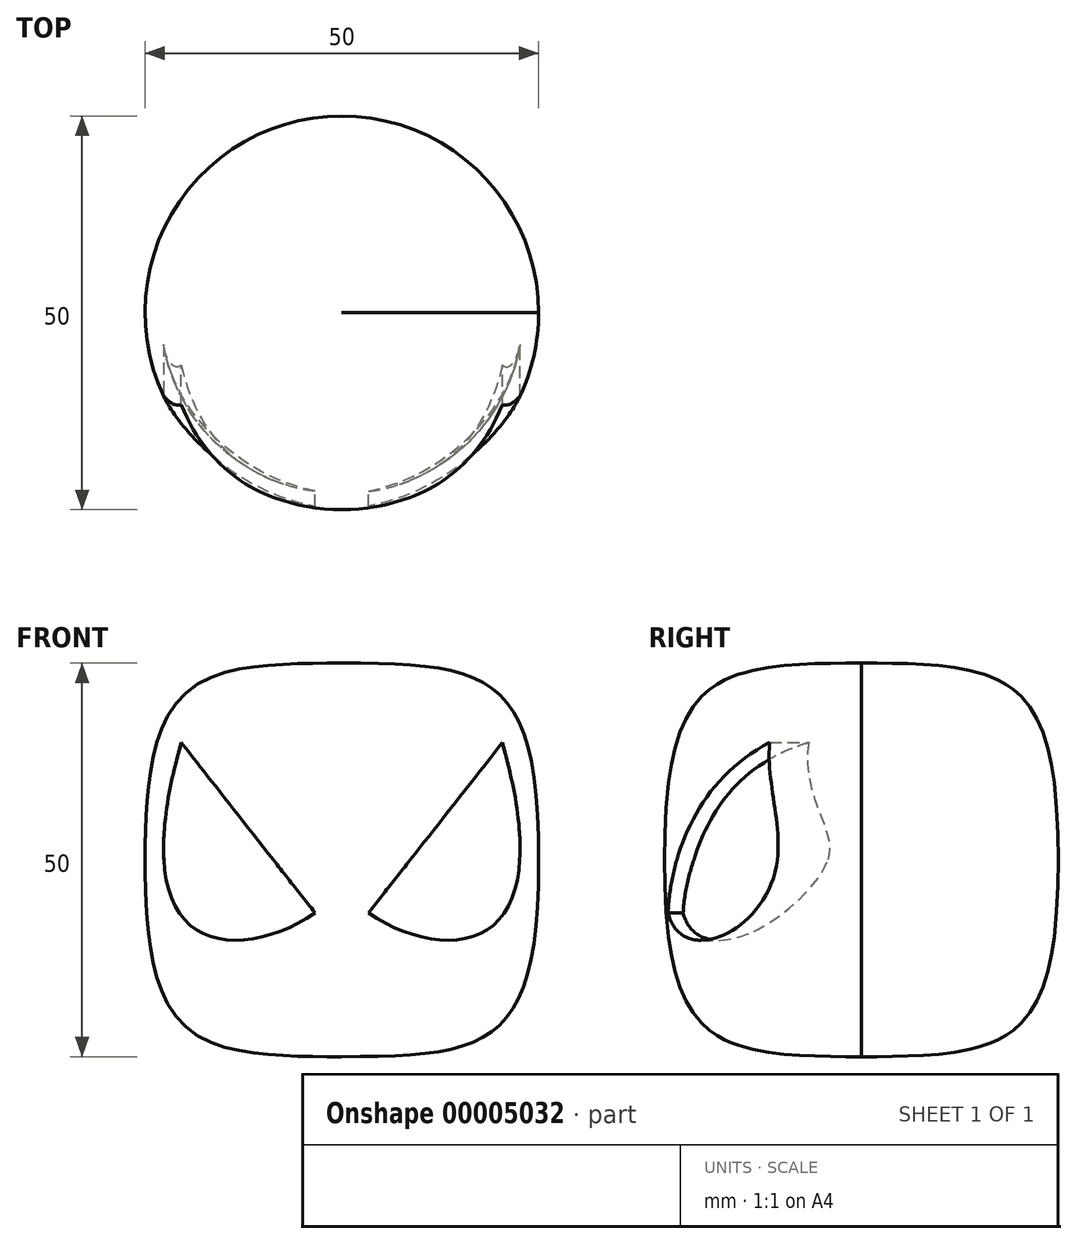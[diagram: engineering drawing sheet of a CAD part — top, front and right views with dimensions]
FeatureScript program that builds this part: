
annotation { "Feature Type Name" : "Feature", "Feature Type Description" : "" }
export const myFeature = defineFeature(function(context is Context, id is Id, definition is map)
    precondition{}
    {
        {
            var Q0;
            Q0=qCreatedBy(makeId("Front.planeOp"),FACE);
            var sketch = newSketch(context, id + "F0", { "sketchPlane" : qUnion([Q0])});
            skLineSegment(sketch, "E0", {"start": v(0, 0) * mm, "end": v(0, 25) * mm, "construction": true});
            skLineSegment(sketch, "E1", {"start": v(0, 0) * mm, "end": v(25, 0) * mm, "construction": true});
            skFitSpline(sketch, "E2", {"points": [v(0, 25) * mm, v(25, 0) * mm], "startDerivative": vector(56.82, 0) * mm, "endDerivative": vector(0, -71.1) * mm});
            skFitSpline(sketch, "E3.0.MirrorCS", {"points": [v(0, -25) * mm, v(25, 0) * mm], "startDerivative": vector(56.82, 0) * mm, "endDerivative": vector(0, 71.1) * mm});
            skLineSegment(sketch, "E4", {"start": v(0, 25) * mm, "end": v(0, -25) * mm});
            skFitSpline(sketch, "E5.0", {"points": [v(0, -23) * mm, v(2.36, -23) * mm, v(6.64, -22.96) * mm, v(10.94, -22.6) * mm, v(13.76, -22.06) * mm, v(15.56, -21.5) * mm, v(17.08, -20.78) * mm, v(18.34, -19.9) * mm, v(19.42, -18.8) * mm, v(20.36, -17.41) * mm, v(21.17, -15.66) * mm, v(22.07, -12.77) * mm, v(22.81, -8.04) * mm, v(23, -2.92) * mm, v(23, 0) * mm]});
            skFitSpline(sketch, "E5.1", {"points": [v(0, 23) * mm, v(2.36, 23) * mm, v(6.64, 22.96) * mm, v(10.94, 22.6) * mm, v(13.76, 22.06) * mm, v(15.56, 21.5) * mm, v(17.08, 20.78) * mm, v(18.34, 19.9) * mm, v(19.42, 18.8) * mm, v(20.36, 17.41) * mm, v(21.17, 15.66) * mm, v(22.07, 12.77) * mm, v(22.81, 8.04) * mm, v(23, 2.92) * mm, v(23, 0) * mm]});
            skSolve(sketch);
        }
        {
            var Q0;
            {var subQ1=sQuery(id+"F0.wireOp",EDGE,"E5.0");Q0=makeQuery(id+"F0.imprint","IMPRINT",FACE,{"disambiguationData":[TD([[makeQuery(id+"F0.imprint","IMPRINT",EDGE,{"derivedFrom":subQ1}),1.0]])]});}
            var Q1;
            {var subQ4=sQuery(id+"F0.wireOp",EDGE,"E2");Q1=makeQuery(id+"F0.imprint","IMPRINT",FACE,{"disambiguationData":[TD([[makeQuery(id+"F0.imprint","IMPRINT",EDGE,{"derivedFrom":subQ4}),-1.0]])]});}
            var Q2;
            Q2=sQuery(id+"F0.wireOp",EDGE,"E4");
            revolve(context, id + "F1", {"entities" : qUnion([Q0, Q1]), "axis" : qUnion([Q2]), "revolveType" : RevolveType.FULL});
        }
        {
            var Q0;
            Q0=qCreatedBy(makeId("Front.planeOp"),FACE);
            var sketch = newSketch(context, id + "F2", { "sketchPlane" : qUnion([Q0])});
            skFitSpline(sketch, "E6", {"points": [v(20.4, 14.89) * mm, v(3.4, -6.73) * mm], "startDerivative": vector(25.57, -89.69) * mm, "endDerivative": vector(-22.96, 16.45) * mm});
            skLineSegment(sketch, "E7", {"start": v(20.4, 14.89) * mm, "end": v(3.4, -6.73) * mm});
            skLineSegment(sketch, "E8.0.MirrorCS", {"start": v(-20.4, 14.89) * mm, "end": v(-3.4, -6.73) * mm});
            skFitSpline(sketch, "E9.0.MirrorCS", {"points": [v(-20.4, 14.89) * mm, v(-3.4, -6.73) * mm], "startDerivative": vector(-25.57, -89.69) * mm, "endDerivative": vector(22.96, 16.45) * mm});
            skSolve(sketch);
        }
        {
            var Q0;
            Q0 = qSketchRegion(id + "F2", true);
            extrude(context, id + "F3", {"entities" : qUnion([Q0]), "operationType" : NewBodyOperationType.REMOVE, "depth" : 25 * mm});
        }
        {
            var Q0;
            {var subQ1=sQuery(id+"F0.wireOp",EDGE,"E5.0");Q0=makeQuery(id+"F0.imprint","IMPRINT",FACE,{"disambiguationData":[TD([[makeQuery(id+"F0.imprint","IMPRINT",EDGE,{"derivedFrom":subQ1}),1.0]])]});}
            var Q1;
            Q1=sQuery(id+"F0.wireOp",EDGE,"E4");
            revolve(context, id + "F4", {"operationType" : NewBodyOperationType.ADD, "entities" : qUnion([Q0]), "axis" : qUnion([Q1]), "revolveType" : RevolveType.FULL});
        }
    });
